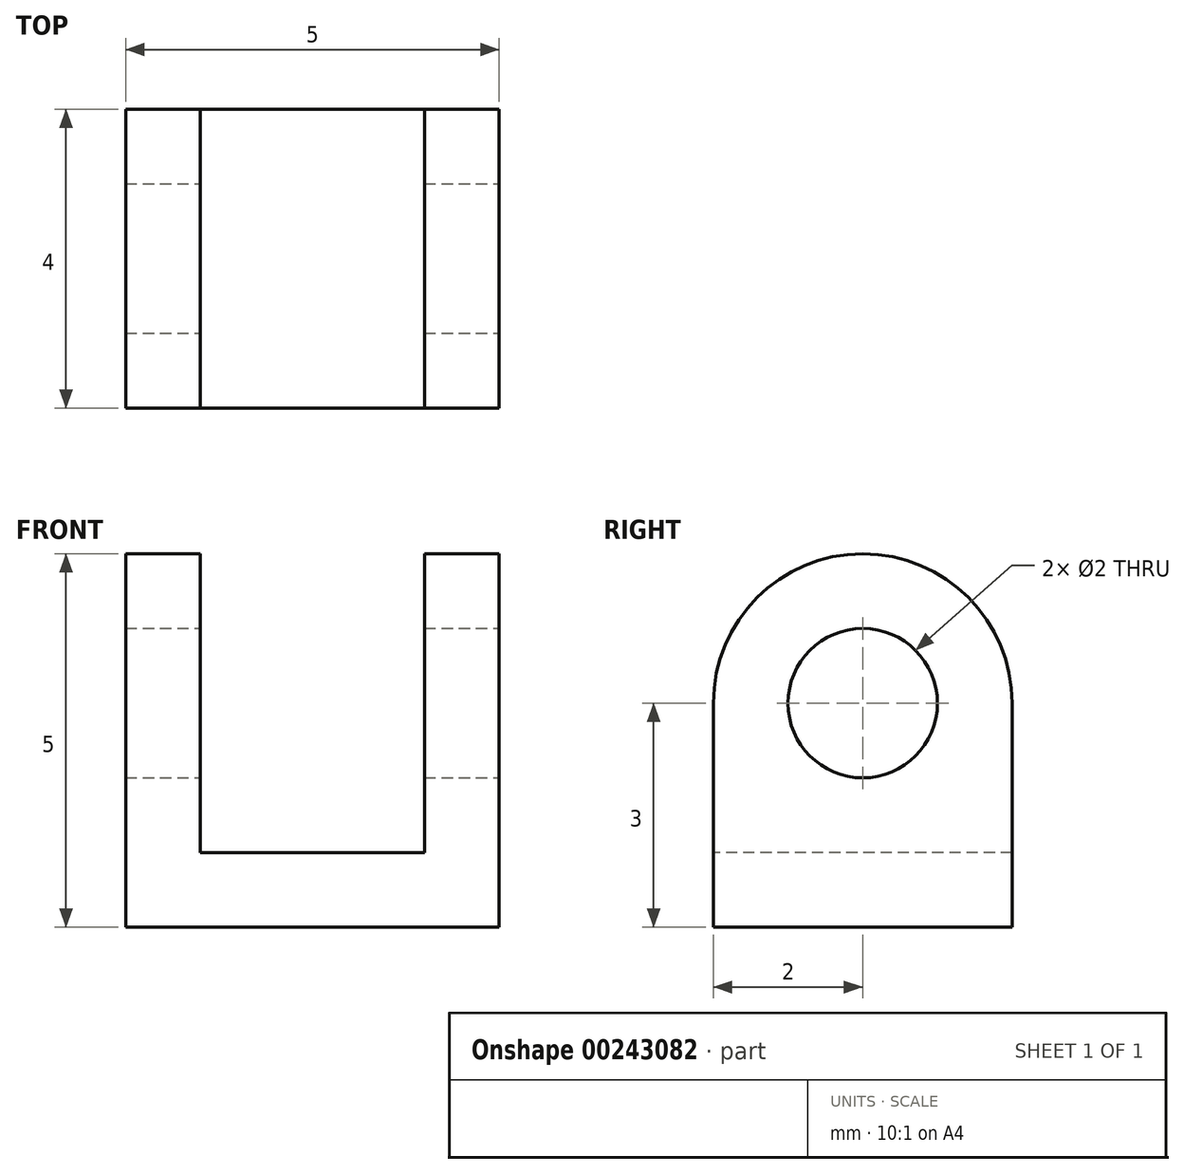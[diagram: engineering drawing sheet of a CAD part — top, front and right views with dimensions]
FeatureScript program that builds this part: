
annotation { "Feature Type Name" : "Feature", "Feature Type Description" : "" }
export const myFeature = defineFeature(function(context is Context, id is Id, definition is map)
    precondition{}
    {
        {
            var Q0;
            Q0=qCreatedBy(makeId("Right.planeOp"),FACE);
            var sketch = newSketch(context, id + "F0", { "sketchPlane" : qUnion([Q0])});
            skLineSegment(sketch, "E0", {"start": v(0, 0) * mm, "end": v(4, 0) * mm});
            skLineSegment(sketch, "E1", {"start": v(4, 0) * mm, "end": v(4, 3) * mm});
            skLineSegment(sketch, "E2", {"start": v(0, 0) * mm, "end": v(0, 3) * mm});
            skArc(sketch, "E3", {"start": v(4, 3) * mm, "mid": v(2, 5) * mm, "end": v(0, 3) * mm});
            skSolve(sketch);
        }
        {
            var Q0;
            Q0 = qSketchRegion(id + "F0", true);
            extrude(context, id + "F1", {"entities" : qUnion([Q0]), "depth" : 5 * mm});
        }
        {
            var Q0;
            Q0=makeQuery(id+"F1.opExtrude","SWEPT_FACE",FACE,{"disambiguationData":[OSD([sQuery(id+"F0.wireOp",EDGE,"E2")])]});
            var sketch = newSketch(context, id + "F2", { "sketchPlane" : qUnion([Q0])});
            skLineSegment(sketch, "E4", {"start": v(0, 0) * mm, "end": v(1, 0) * mm});
            skLineSegment(sketch, "E5", {"start": v(1, 0) * mm, "end": v(1, 1) * mm});
            skLineSegment(sketch, "E6.bottom", {"start": v(1, 1) * mm, "end": v(4, 1) * mm});
            skLineSegment(sketch, "E6.top", {"start": v(1, 5) * mm, "end": v(4, 5) * mm});
            skLineSegment(sketch, "E6.left", {"start": v(1, 1) * mm, "end": v(1, 5) * mm});
            skLineSegment(sketch, "E6.right", {"start": v(4, 1) * mm, "end": v(4, 5) * mm});
            skSolve(sketch);
        }
        {
            var Q0;
            Q0 = qSketchRegion(id + "F2", true);
            extrude(context, id + "F3", {"entities" : qUnion([Q0]), "operationType" : NewBodyOperationType.REMOVE, "oppositeDirection" : true, "depth" : 4 * mm});
        }
        {
            var Q0;
            Q0=makeQuery(id+"F1.opExtrude","CAP_FACE",FACE,{"disambiguationData":[OSD([sQuery(id+"F0.wireOp",EDGE,"E0"),sQuery(id+"F0.wireOp",EDGE,"E1"),sQuery(id+"F0.wireOp",EDGE,"E2"),sQuery(id+"F0.wireOp",EDGE,"E3")])],"isStart":false});
            var sketch = newSketch(context, id + "F4", { "sketchPlane" : qUnion([Q0])});
            skCircle(sketch, "E7", {"center": v(2, 3) * mm, "radius": 1 * mm});
            skSolve(sketch);
        }
        {
            var Q0;
            Q0 = qSketchRegion(id + "F4", true);
            extrude(context, id + "F5", {"entities" : qUnion([Q0]), "operationType" : NewBodyOperationType.REMOVE, "oppositeDirection" : true, "depth" : 5 * mm});
        }
    });
